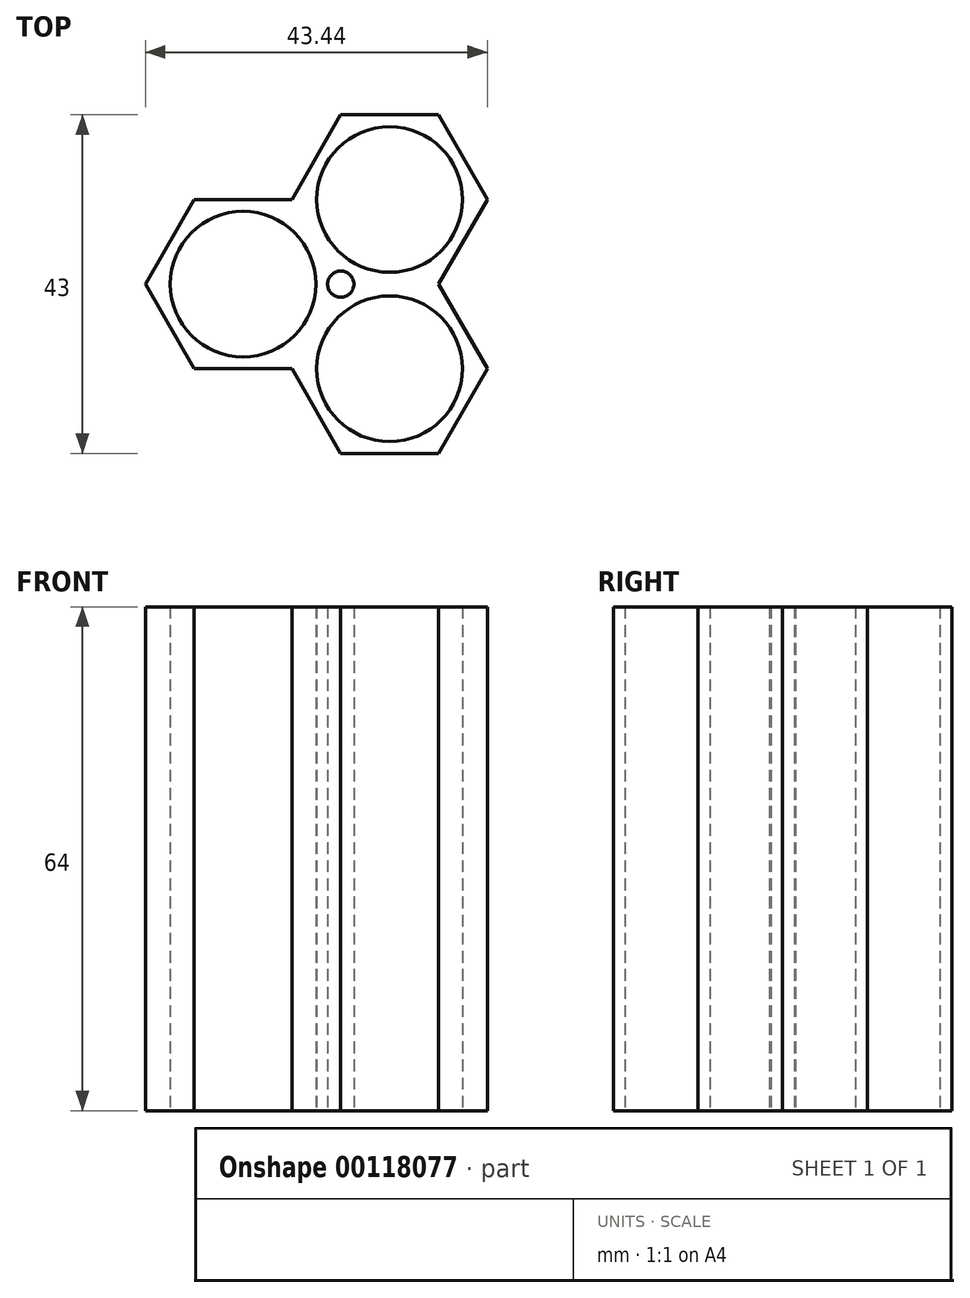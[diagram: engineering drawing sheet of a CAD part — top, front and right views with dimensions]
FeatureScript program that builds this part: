
annotation { "Feature Type Name" : "Feature", "Feature Type Description" : "" }
export const myFeature = defineFeature(function(context is Context, id is Id, definition is map)
    precondition{}
    {
        {
            var Q0;
            Q0=qCreatedBy(makeId("Top.planeOp"),FACE);
            var sketch = newSketch(context, id + "F0", { "sketchPlane" : qUnion([Q0])});
            skCircle(sketch, "E0.cCircle", {"center": v(0, 0) * mm, "radius": 10.75 * mm, "construction": true});
            skLineSegment(sketch, "E0.0", {"start": v(-6.2, 10.75) * mm, "end": v(6.2, 10.75) * mm});
            skLineSegment(sketch, "E0.1", {"start": v(6.2, 10.75) * mm, "end": v(12.41, 0) * mm});
            skLineSegment(sketch, "E0.2", {"start": v(12.41, 0) * mm, "end": v(6.2, -10.75) * mm});
            skLineSegment(sketch, "E0.3", {"start": v(6.2, -10.75) * mm, "end": v(-6.2, -10.75) * mm});
            skLineSegment(sketch, "E0.4", {"start": v(-6.2, -10.75) * mm, "end": v(-12.41, 0) * mm});
            skLineSegment(sketch, "E0.5", {"start": v(-12.41, 0) * mm, "end": v(-6.2, 10.75) * mm});
            skPoint(sketch, "E0.0.midPoint", {"position": v(0, 10.75) * mm});
            skCircle(sketch, "E1.cCircle", {"center": v(18.62, 10.75) * mm, "radius": 10.75 * mm, "construction": true});
            skLineSegment(sketch, "E1.0", {"start": v(24.83, 0) * mm, "end": v(12.41, 0) * mm});
            skLineSegment(sketch, "E1.1", {"start": v(12.41, 0) * mm, "end": v(6.2, 10.75) * mm});
            skLineSegment(sketch, "E1.2", {"start": v(6.2, 10.75) * mm, "end": v(12.41, 21.5) * mm});
            skLineSegment(sketch, "E1.3", {"start": v(12.41, 21.5) * mm, "end": v(24.83, 21.5) * mm});
            skLineSegment(sketch, "E1.4", {"start": v(24.83, 21.5) * mm, "end": v(31.03, 10.75) * mm});
            skLineSegment(sketch, "E1.5", {"start": v(31.03, 10.75) * mm, "end": v(24.83, 0) * mm});
            skPoint(sketch, "E1.0.midPoint", {"position": v(18.62, 0) * mm});
            skCircle(sketch, "E2.cCircle", {"center": v(18.62, -10.75) * mm, "radius": 10.75 * mm, "construction": true});
            skLineSegment(sketch, "E2.0", {"start": v(12.41, 0) * mm, "end": v(24.83, 0) * mm});
            skLineSegment(sketch, "E2.1", {"start": v(24.83, 0) * mm, "end": v(31.03, -10.75) * mm});
            skLineSegment(sketch, "E2.2", {"start": v(31.03, -10.75) * mm, "end": v(24.83, -21.5) * mm});
            skLineSegment(sketch, "E2.3", {"start": v(24.83, -21.5) * mm, "end": v(12.41, -21.5) * mm});
            skLineSegment(sketch, "E2.4", {"start": v(12.41, -21.5) * mm, "end": v(6.2, -10.75) * mm});
            skLineSegment(sketch, "E2.5", {"start": v(6.2, -10.75) * mm, "end": v(12.41, 0) * mm});
            skCircle(sketch, "E3", {"center": v(18.62, -10.75) * mm, "radius": 9.25 * mm});
            skCircle(sketch, "E4", {"center": v(0, 0) * mm, "radius": 9.25 * mm});
            skCircle(sketch, "E5", {"center": v(18.62, 10.75) * mm, "radius": 9.25 * mm});
            skCircle(sketch, "E6", {"center": v(12.41, 0) * mm, "radius": 1.66 * mm});
            skSolve(sketch);
        }
        {
            var Q0;
            Q0=makeQuery(id+"F0.imprint","IMPRINT",FACE,{"disambiguationData":[TD([[makeQuery(id+"F0.imprint","IMPRINT",EDGE,{"derivedFrom":sQuery(id+"F0.wireOp",EDGE,"E0.0")}),-1.0]])]});
            var Q1;
            {var subQ5=sQuery(id+"F0.wireOp",EDGE,"E1.2");Q1=makeQuery(id+"F0.imprint","IMPRINT",FACE,{"disambiguationData":[TD([[makeQuery(id+"F0.imprint","IMPRINT",EDGE,{"derivedFrom":subQ5}),-1.0]])]});}
            var Q2;
            {var subQ0=sQuery(id+"F0.wireOp",EDGE,"E2.1");Q2=makeQuery(id+"F0.imprint","IMPRINT",FACE,{"disambiguationData":[TD([[makeQuery(id+"F0.imprint","IMPRINT",EDGE,{"derivedFrom":subQ0}),-1.0]])]});}
            extrude(context, id + "F1", {"entities" : qUnion([Q0, Q1, Q2]), "depth" : 64 * mm});
        }
    });
